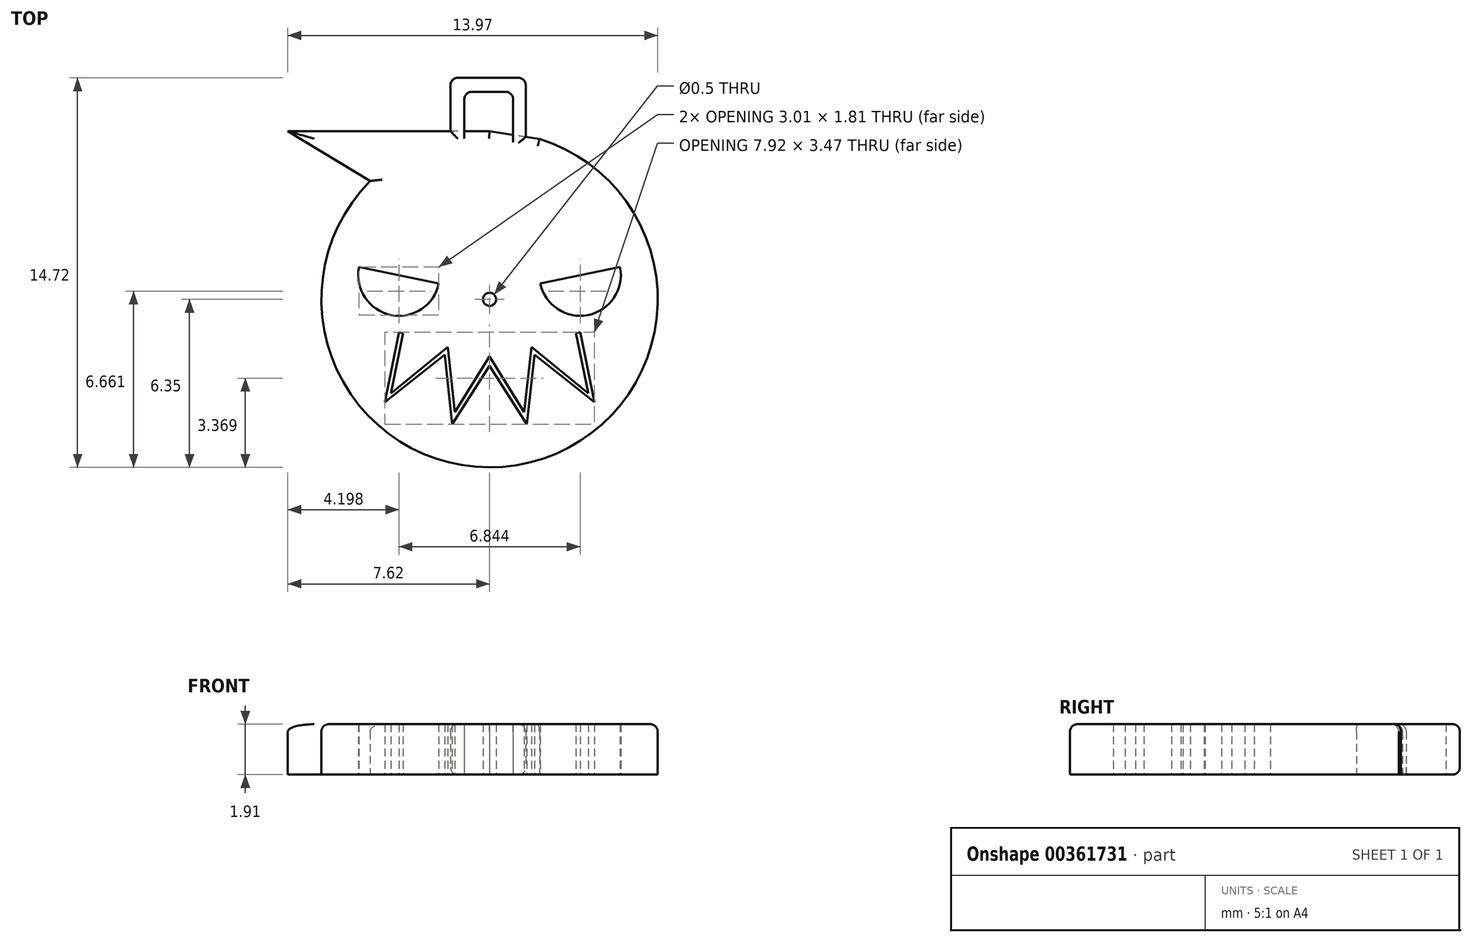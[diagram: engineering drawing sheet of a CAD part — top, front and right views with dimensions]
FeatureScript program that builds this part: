
annotation { "Feature Type Name" : "Feature", "Feature Type Description" : "" }
export const myFeature = defineFeature(function(context is Context, id is Id, definition is map)
    precondition{}
    {
        {
            var Q0;
            Q0=qCreatedBy(makeId("Top.planeOp"),FACE);
            var sketch = newSketch(context, id + "F0", { "sketchPlane" : qUnion([Q0])});
            skArc(sketch, "E0", {"start": v(-4.5, 4.47) * mm, "mid": v(1.54, -6.16) * mm, "end": v(1.88, 6.06) * mm});
            skLineSegment(sketch, "E1", {"start": v(-1.9, 6.35) * mm, "end": v(-7.62, 6.35) * mm});
            skLineSegment(sketch, "E2", {"start": v(-4.5, 4.47) * mm, "end": v(-7.62, 6.35) * mm});
            skCircle(sketch, "E3", {"center": v(0, 0) * mm, "radius": 0.25 * mm});
            skArc(sketch, "E4", {"start": v(-4.93, 1.22) * mm, "mid": v(-3.73, -0.6) * mm, "end": v(-1.92, 0.6) * mm});
            skArc(sketch, "E5.MirrorC", {"start": v(4.93, 1.22) * mm, "mid": v(3.73, -0.6) * mm, "end": v(1.92, 0.6) * mm});
            skLineSegment(sketch, "E6", {"start": v(-4.93, 1.22) * mm, "end": v(-1.92, 0.6) * mm});
            skLineSegment(sketch, "E7.MirrorCS", {"start": v(4.93, 1.22) * mm, "end": v(1.92, 0.6) * mm});
            skLineSegment(sketch, "E8", {"start": v(-3.26, -1.28) * mm, "end": v(-3.73, -3.56) * mm});
            skLineSegment(sketch, "E9", {"start": v(-3.73, -3.56) * mm, "end": v(-1.58, -1.8) * mm});
            skLineSegment(sketch, "E10", {"start": v(-1.58, -1.8) * mm, "end": v(-1.3, -4.27) * mm});
            skLineSegment(sketch, "E11", {"start": v(-1.3, -4.27) * mm, "end": v(0, -2.16) * mm});
            skLineSegment(sketch, "E12.MirrorCS", {"start": v(1.3, -4.27) * mm, "end": v(0, -2.16) * mm});
            skLineSegment(sketch, "E13.MirrorCS", {"start": v(1.58, -1.8) * mm, "end": v(1.3, -4.27) * mm});
            skLineSegment(sketch, "E14.MirrorCS", {"start": v(3.73, -3.56) * mm, "end": v(1.58, -1.8) * mm});
            skLineSegment(sketch, "E15.MirrorCS", {"start": v(3.26, -1.28) * mm, "end": v(3.73, -3.56) * mm});
            skLineSegment(sketch, "E16", {"start": v(-3.26, -1.28) * mm, "end": v(-3.42, -1.24) * mm});
            skLineSegment(sketch, "E17", {"start": v(-3.42, -1.24) * mm, "end": v(-3.96, -3.88) * mm});
            skLineSegment(sketch, "E18", {"start": v(-3.96, -3.88) * mm, "end": v(-1.7, -2.09) * mm});
            skLineSegment(sketch, "E19", {"start": v(-1.7, -2.09) * mm, "end": v(-1.4, -4.72) * mm});
            skLineSegment(sketch, "E20", {"start": v(-1.4, -4.72) * mm, "end": v(0, -2.52) * mm});
            skLineSegment(sketch, "E21.MirrorCS", {"start": v(1.4, -4.72) * mm, "end": v(0, -2.52) * mm});
            skLineSegment(sketch, "E22.MirrorCS", {"start": v(1.7, -2.09) * mm, "end": v(1.4, -4.72) * mm});
            skLineSegment(sketch, "E23.MirrorCS", {"start": v(3.96, -3.88) * mm, "end": v(1.7, -2.09) * mm});
            skLineSegment(sketch, "E24.MirrorCS", {"start": v(3.42, -1.24) * mm, "end": v(3.96, -3.88) * mm});
            skLineSegment(sketch, "E25.MirrorCS", {"start": v(3.26, -1.28) * mm, "end": v(3.42, -1.24) * mm});
            skPoint(sketch, "E26.center.orphan", {"position": v(0, 6.35) * mm});
            skLineSegment(sketch, "E27", {"start": v(1.88, 6.06) * mm, "end": v(0, 6.35) * mm});
            skLineSegment(sketch, "E28", {"start": v(-1.9, 6.35) * mm, "end": v(0, 6.35) * mm});
            skLineSegment(sketch, "E29", {"start": v(-0.95, 6.35) * mm, "end": v(-0.95, 7.56) * mm});
            skLineSegment(sketch, "E30", {"start": v(-0.67, 7.84) * mm, "end": v(0.6, 7.84) * mm});
            skLineSegment(sketch, "E31", {"start": v(0.89, 7.56) * mm, "end": v(0.89, 6.22) * mm});
            skLineSegment(sketch, "E32", {"start": v(-1.48, 6.35) * mm, "end": v(-1.48, 8.1) * mm});
            skLineSegment(sketch, "E33", {"start": v(-1.2, 8.37) * mm, "end": v(1.08, 8.37) * mm});
            skLineSegment(sketch, "E34", {"start": v(1.37, 8.1) * mm, "end": v(1.37, 6.14) * mm});
            skPoint(sketch, "E35.visualSharp", {"position": v(-1.48, 8.37) * mm});
            skArc(sketch, "E35.filletArc", {"start": v(-1.2, 8.37) * mm, "mid": v(-1.4, 8.3) * mm, "end": v(-1.48, 8.1) * mm});
            skPoint(sketch, "E36.visualSharp", {"position": v(1.37, 8.37) * mm});
            skArc(sketch, "E36.filletArc", {"start": v(1.37, 8.1) * mm, "mid": v(1.28, 8.3) * mm, "end": v(1.08, 8.37) * mm});
            skPoint(sketch, "E37.visualSharp", {"position": v(-0.95, 7.84) * mm});
            skArc(sketch, "E37.filletArc", {"start": v(-0.67, 7.84) * mm, "mid": v(-0.87, 7.76) * mm, "end": v(-0.95, 7.56) * mm});
            skPoint(sketch, "E38.visualSharp", {"position": v(0.89, 7.84) * mm});
            skArc(sketch, "E38.filletArc", {"start": v(0.89, 7.56) * mm, "mid": v(0.8, 7.76) * mm, "end": v(0.6, 7.84) * mm});
            skSolve(sketch);
        }
        {
            var Q0;
            Q0=makeQuery(id+"F0.imprint","IMPRINT",FACE,{"disambiguationData":[TD([[makeQuery(id+"F0.imprint","IMPRINT",EDGE,{"derivedFrom":sQuery(id+"F0.wireOp",EDGE,"E0")}),1.0]])]});
            var Q1;
            {var subQ0=sQuery(id+"F0.wireOp",EDGE,"E29");Q1=makeQuery(id+"F0.imprint","IMPRINT",FACE,{"disambiguationData":[TD([[makeQuery(id+"F0.imprint","IMPRINT",EDGE,{"derivedFrom":subQ0}),1.0]])]});}
            extrude(context, id + "F1", {"entities" : qUnion([Q0, Q1]), "depth" : 1.9 * mm});
        }
        {
            var Q0;
            Q0=makeQuery(id+"F0.imprint","IMPRINT",FACE,{"disambiguationData":[TD([[makeQuery(id+"F0.imprint","IMPRINT",EDGE,{"derivedFrom":sQuery(id+"F0.wireOp",EDGE,"E4")}),1.0]])]});
            var Q1;
            Q1=makeQuery(id+"F0.imprint","IMPRINT",FACE,{"disambiguationData":[TD([[makeQuery(id+"F0.imprint","IMPRINT",EDGE,{"derivedFrom":sQuery(id+"F0.wireOp",EDGE,"E5.MirrorC")}),-1.0]])]});
            var Q2;
            Q2=makeQuery(id+"F0.imprint","IMPRINT",FACE,{"disambiguationData":[TD([[makeQuery(id+"F0.imprint","IMPRINT",EDGE,{"derivedFrom":sQuery(id+"F0.wireOp",EDGE,"E3")}),1.0]])]});
            var Q3;
            Q3=makeQuery(id+"F0.imprint","IMPRINT",FACE,{"disambiguationData":[TD([[makeQuery(id+"F0.imprint","IMPRINT",EDGE,{"derivedFrom":sQuery(id+"F0.wireOp",EDGE,"E8")}),-1.0]])]});
            var Q4;
            {var subQ3=sQuery(id+"F0.wireOp",EDGE,"vlUMOEfx-GRlx-MxnO-jUKY-hXm5ggsJFdDv");Q4=makeQuery(id+"F0.imprint","IMPRINT",FACE,{"disambiguationData":[TD([[makeQuery(id+"F0.imprint","IMPRINT",EDGE,{"derivedFrom":subQ3}),1.0]])]});}
            extrude(context, id + "F2", {"entities" : qUnion([Q0, Q1, Q2, Q3, Q4]), "operationType" : NewBodyOperationType.REMOVE, "oppositeDirection" : true, "depth" : 1.9 * mm});
        }
        {
            var Q0;
            Q0=makeQuery(id+"F1.opExtrude","CAP_EDGE",EDGE,{"disambiguationData":[OSD([sQuery(id+"F0.wireOp",EDGE,"E33")])],"isStart":true});
            var Q1;
            Q1=makeQuery(id+"F1.opExtrude","CAP_EDGE",EDGE,{"disambiguationData":[OSD([sQuery(id+"F0.wireOp",EDGE,"E33")])],"isStart":false});
            var Q2;
            Q2=makeQuery(id+"F1.opExtrude","CAP_EDGE",EDGE,{"disambiguationData":[OSD([sQuery(id+"F0.wireOp",EDGE,"E1"),sQuery(id+"F0.wireOp",EDGE,"E28")])],"isStart":false});
            var Q3;
            Q3=makeQuery(id+"F1.opExtrude","CAP_EDGE",EDGE,{"disambiguationData":[OSD([sQuery(id+"F0.wireOp",EDGE,"E2")])],"isStart":false});
            var Q4;
            Q4=makeQuery(id+"F1.opExtrude","CAP_EDGE",EDGE,{"disambiguationData":[OSD([sQuery(id+"F0.wireOp",EDGE,"E0")])],"isStart":false});
            var Q5;
            {var subQ0=sQuery(id+"F0.wireOp",EDGE,"E27");Q5=makeQuery(id+"F1.opExtrude","CAP_EDGE",EDGE,{"disambiguationData":[OSD([subQ0]),TDD([makeQuery(id+"F0.imprint","IMPRINT",EDGE,{"disambiguationData":[TD([[makeQuery(id+"F0.imprint","INTERSECT",VERTEX,{"derivedFrom":[sQuery(id+"F0.wireOp",EDGE,"E0"),subQ0]}),-1.0]])],"derivedFrom":subQ0})])],"isStart":false});}
            var Q6;
            {var subQ0=sQuery(id+"F0.wireOp",EDGE,"E27");Q6=makeQuery(id+"F1.opExtrude","CAP_EDGE",EDGE,{"disambiguationData":[OSD([subQ0]),TDD([makeQuery(id+"F0.imprint","IMPRINT",EDGE,{"disambiguationData":[TD([[makeQuery(id+"F0.imprint","INTERSECT",VERTEX,{"derivedFrom":[subQ0,sQuery(id+"F0.wireOp",EDGE,"E28")]}),1.0]])],"derivedFrom":subQ0})])],"isStart":false});}
            var Q7;
            Q7=makeQuery(id+"F1.opExtrude","CAP_EDGE",EDGE,{"disambiguationData":[OSD([sQuery(id+"F0.wireOp",EDGE,"E28")])],"isStart":false});
            fillet(context, id + "F3", {"entities" : qUnion([Q0, Q1, Q2, Q3, Q4, Q5, Q6, Q7]), "radius" : 0.28 * mm, "tangentPropagation" : true, "allowEdgeOverflow" : false});
        }
    });
